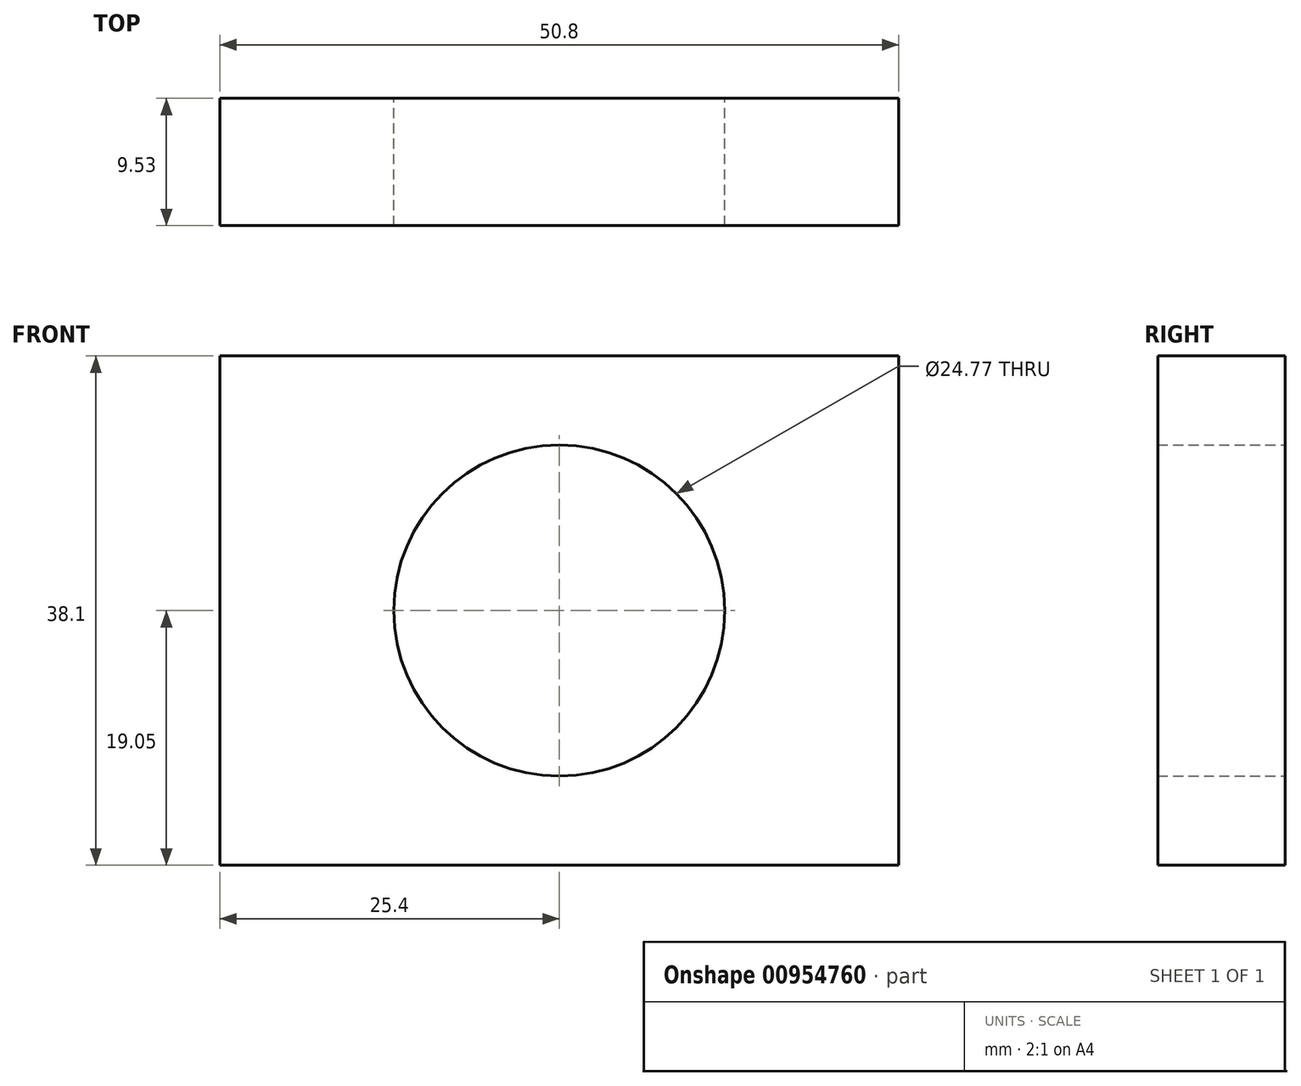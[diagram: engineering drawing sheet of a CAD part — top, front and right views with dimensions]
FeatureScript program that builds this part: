
annotation { "Feature Type Name" : "Feature", "Feature Type Description" : "" }
export const myFeature = defineFeature(function(context is Context, id is Id, definition is map)
    precondition{}
    {
        {
            var Q0;
            Q0=qCreatedBy(makeId("Front.planeOp"),FACE);
            var sketch = newSketch(context, id + "F0", { "sketchPlane" : qUnion([Q0])});
            skLineSegment(sketch, "E0.bottom", {"start": v(-25.4, -19.05) * mm, "end": v(25.4, -19.05) * mm});
            skLineSegment(sketch, "E0.top", {"start": v(-25.4, 19.05) * mm, "end": v(25.4, 19.05) * mm});
            skLineSegment(sketch, "E0.left", {"start": v(-25.4, -19.05) * mm, "end": v(-25.4, 19.05) * mm});
            skLineSegment(sketch, "E0.right", {"start": v(25.4, -19.05) * mm, "end": v(25.4, 19.05) * mm});
            skCircle(sketch, "E1", {"center": v(0, 0) * mm, "radius": 12.38 * mm});
            skSolve(sketch);
        }
        {
            var Q0;
            Q0=makeQuery(id+"F0.imprint","IMPRINT",FACE,{"disambiguationData":[TD([[makeQuery(id+"F0.imprint","IMPRINT",EDGE,{"derivedFrom":sQuery(id+"F0.wireOp",EDGE,"E0.bottom")}),1.0]])]});
            extrude(context, id + "F1", {"entities" : qUnion([Q0]), "depth" : 9.52 * mm, "offsetDistance" : 25.4 * mm});
        }
    });
